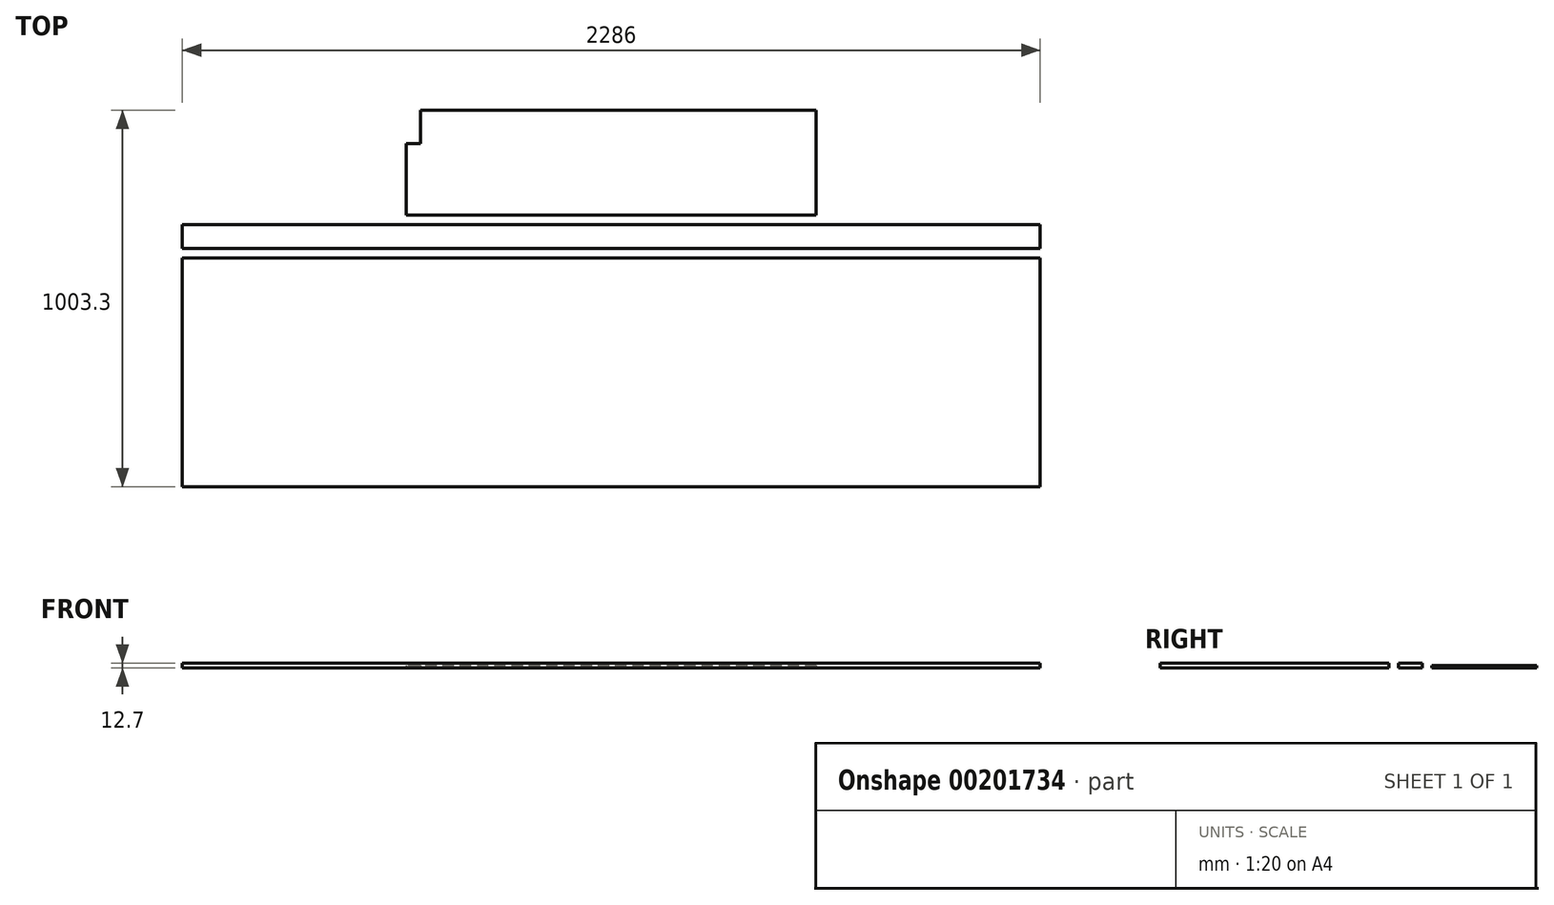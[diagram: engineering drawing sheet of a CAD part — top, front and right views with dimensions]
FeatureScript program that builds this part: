
annotation { "Feature Type Name" : "Feature", "Feature Type Description" : "" }
export const myFeature = defineFeature(function(context is Context, id is Id, definition is map)
    precondition{}
    {
        {
            var Q0;
            Q0=qCreatedBy(makeId("Top.planeOp"),FACE);
            var sketch = newSketch(context, id + "F0", { "sketchPlane" : qUnion([Q0])});
            skLineSegment(sketch, "E0.bottom", {"start": v(1143, -304.8) * mm, "end": v(-1143, -304.8) * mm});
            skLineSegment(sketch, "E0.top", {"start": v(1143, 304.8) * mm, "end": v(-1143, 304.8) * mm});
            skLineSegment(sketch, "E0.left", {"start": v(1143, -304.8) * mm, "end": v(1143, 304.8) * mm});
            skLineSegment(sketch, "E0.right", {"start": v(-1143, -304.8) * mm, "end": v(-1143, 304.8) * mm});
            skPoint(sketch, "E0.middle", {"position": v(0, 0) * mm});
            skSolve(sketch);
        }
        {
            var Q0;
            Q0=makeQuery(id+"F0.imprint","IMPRINT",FACE,{"disambiguationData":[TD([[makeQuery(id+"F0.imprint","IMPRINT",EDGE,{"derivedFrom":sQuery(id+"F0.wireOp",EDGE,"E0.bottom")}),-1.0]])]});
            extrude(context, id + "F1", {"entities" : qUnion([Q0]), "depth" : 12.7 * mm});
        }
        {
            var Q0;
            Q0=qCreatedBy(makeId("Top.planeOp"),FACE);
            var sketch = newSketch(context, id + "F2", { "sketchPlane" : qUnion([Q0])});
            skLineSegment(sketch, "E1.bottom", {"start": v(1143, 393.7) * mm, "end": v(-1143, 393.7) * mm});
            skLineSegment(sketch, "E1.top", {"start": v(1143, 330.2) * mm, "end": v(-1143, 330.2) * mm});
            skLineSegment(sketch, "E1.left", {"start": v(1143, 393.7) * mm, "end": v(1143, 330.2) * mm});
            skLineSegment(sketch, "E1.right", {"start": v(-1143, 393.7) * mm, "end": v(-1143, 330.2) * mm});
            skPoint(sketch, "E1.middle", {"position": v(0, 361.95) * mm});
            skSolve(sketch);
        }
        {
            var Q0;
            Q0=makeQuery(id+"F2.imprint","IMPRINT",FACE,{"disambiguationData":[TD([[makeQuery(id+"F2.imprint","IMPRINT",EDGE,{"derivedFrom":sQuery(id+"F2.wireOp",EDGE,"E1.bottom")}),1.0]])]});
            var Q1;
            Q1=makeQuery(id+"F1.opExtrude","CAP_FACE",FACE,{"disambiguationData":[OSD([sQuery(id+"F0.wireOp",EDGE,"E0.bottom"),sQuery(id+"F0.wireOp",EDGE,"E0.top"),sQuery(id+"F0.wireOp",EDGE,"E0.left"),sQuery(id+"F0.wireOp",EDGE,"E0.right")])],"isStart":false});
            extrude(context, id + "F3", {"entities" : qUnion([Q0]), "endBound" : BoundingType.UP_TO_SURFACE, "endBoundEntityFace" : qUnion([Q1]), "depth" : 25.4 * mm});
        }
        {
            var Q0;
            Q0=qCreatedBy(makeId("Top.planeOp"),FACE);
            var sketch = newSketch(context, id + "F4", { "sketchPlane" : qUnion([Q0])});
            skLineSegment(sketch, "E2.bottom", {"start": v(546.1, 698.5) * mm, "end": v(-508, 698.5) * mm});
            skLineSegment(sketch, "E2.top", {"start": v(546.1, 419.1) * mm, "end": v(-546.1, 419.1) * mm});
            skLineSegment(sketch, "E2.left", {"start": v(546.1, 698.5) * mm, "end": v(546.1, 419.1) * mm});
            skLineSegment(sketch, "E2.right", {"start": v(-546.1, 609.6) * mm, "end": v(-546.1, 419.1) * mm});
            skPoint(sketch, "E2.middle", {"position": v(0, 558.8) * mm});
            skLineSegment(sketch, "E3", {"start": v(-508, 698.5) * mm, "end": v(-508, 609.6) * mm});
            skLineSegment(sketch, "E4", {"start": v(-508, 609.6) * mm, "end": v(-546.1, 609.6) * mm});
            skSolve(sketch);
        }
        {
            var Q0;
            Q0=makeQuery(id+"F4.imprint","IMPRINT",FACE,{"disambiguationData":[TD([[makeQuery(id+"F4.imprint","IMPRINT",EDGE,{"derivedFrom":sQuery(id+"F4.wireOp",EDGE,"E2.bottom")}),1.0]])]});
            extrude(context, id + "F5", {"entities" : qUnion([Q0]), "depth" : 6.35 * mm});
        }
    });
